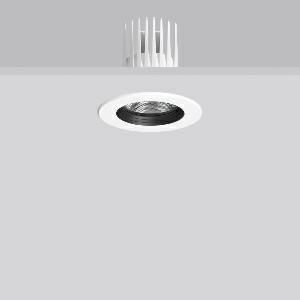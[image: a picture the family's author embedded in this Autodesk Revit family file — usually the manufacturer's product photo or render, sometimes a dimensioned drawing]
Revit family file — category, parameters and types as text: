
# Revit family: heledon_mini_e_901740_002_3_76_0c1c
name_source: partatom
category: Lighting Fixtures
units: mm (PartAtom-declared; Revit-internal decimal feet)

## family parameters
Cut with Voids When Loaded = No
Host = Face
Light Source = No
Part Type = Normal
Room Calculation Point = No
Round Connector Dimension = Use Diameter
Shared = No

## types (1)
- HELEDON mini E (1 x LED Modul 935, 2600 lm, 3500)
    Apparent Load = 20 VA
    Approval mark = CE
    CIE Flux Codes = 100 100 100 100 100
    Color Rendering = 92
    Color Temperature = 3500
    Default Elevation = 1800 mm
    Description = Series: HELEDON mini
Round recessed downlight. Housing: die-cast aluminium, powder-coated. Black plastic ring and recessed LED to prevent glare from the side. Optical assembly with reflector made of MIRO-Silver with 98% total light reflection for outstanding efficiency - can be changed without tools. Best colour rendering index Ra>90. Suitable for Recessed ceiling mounting. Installation without tools thanks to spring fastening system. Including separate LED converter with connecting cable 600 mm.High quality converter without flickering and stroboscopic effect. Through-wiring box (5 pole) available as accessory. The following accessories can be mounted without use of tools: interchangeable lenses, decorative glasses, honeycomb louvre, clear and frosted diffusers, white interchangeable plastic ring. 
Colour: traffic white, matt (RAL 9016)
Diameter: 124 mm
Height: 3 mm
Cut-out diameter: 114 mm
Recess height: 170 mm
Luminaire: recess height: 120 mm
Lamp: LED
Socket: without socket
Colour temperature: 3500K
Colour rendering index (CRI): 92
System power: 20 W
Rated luminous flux: 2600 lm
Luminous efficiency: 130 lm/W
Control gear: Converter, dimmable, DALI
Protection class: II
Type of protection: IP 20
    Height = 0 mm  [stored 0 ft]
    Lamp = 1 x LED Modul 935
    Lamp Light Flux = 2600 lm
    Lamp count = 1
    Length = 124 mm  [stored 0.406824 ft]
    Lifetime = 50000 h
    Luminous efficacy = 130 lm/W
    Manufacturer = RZB
    ModVariant = No
    Model = 901740.002.3.76
    Mounting Place = Ceiling
    Mounting Type = Recessed
    Number of Poles = 1
    OnlyDefault = Yes
    Power Factor = 1
    Product Name = HELEDON mini E
    Product group = Recessed downlights
    ProductGroupID = 402
    Protection Class = Protection class II
    Protection Degree = IP 20
    RLX_Detail_Level = 1
    RLX_Emergency_Light_Flux = 0 lm
    RLX_Emergency_Type = 0
    RLX_Emergency_Type_DB = No
    RlxData = <blob elided: 126401 chars, md5=7cba44b6>
    Socket = socket
    Standby Power = 0 W
    System Light Flux = 2600 lm
    System Power = 20 W
    Type Comments = Product without accessories
    Type Image = 901657.002.jpg
    URL = http://relux.com
    VarID = ---
    Voltage = 230 V
    Voltage Range = 220-240 V
    Weight = 0.00 kg
    Width = 0 mm  [stored 0 ft]

note: [stored X ft] marks values corroborated as IEEE doubles in the binary element streams (Revit-internal decimal feet)

## geometry (parser evidence)
native form markers: Blend x4, Sweep x11
no freeform markers — native parametric forms only
